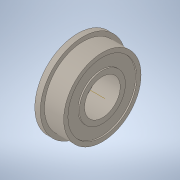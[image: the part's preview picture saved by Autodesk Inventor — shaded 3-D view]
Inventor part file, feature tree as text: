
AUTODESK INVENTOR PART (.ipt)
format: ipt  version: 2022.3 (Build 263350000, 350)  size: 156,672 bytes
history: native  units: in
note: dims shown in document units (in); Inventor stores cm internally (conversion verified against a paired STEP export)
features: revolve x2, sketch x1
ambient origin geometry x8: Origin, YZ Plane, XZ Plane, XY Plane, X Axis, Y Axis, Z Axis, Center Point
bodies: Solid1 (feature_tree)
feature tree (3):
  revolve  "Revolution1"  [1 undecoded]
  sketch  "Sketch1"  dims[d0=90.0deg]
  revolve  "Revolve1"  [1 undecoded]
note: 2 required parameter values undecoded (feature->parameter linkage not recoverable at this tier; creation-order binding heuristic only, values carry confidence <= 0.55)
